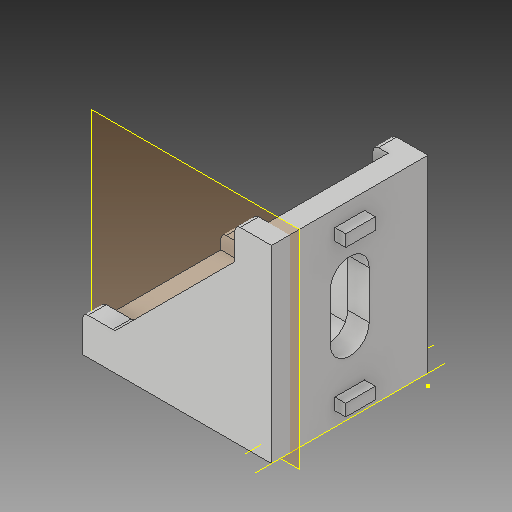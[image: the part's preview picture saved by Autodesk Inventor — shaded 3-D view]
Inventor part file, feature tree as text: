
AUTODESK INVENTOR PART (.ipt)
format: ipt  version: 2018 (Build 220112000, 112)  size: 184,832 bytes
history: native  units: mm
features: sketch x7, other x5, plane x1
ambient origin geometry x8: Origin, YZ Plane, XZ Plane, XY Plane, X Axis, Y Axis, Z Axis, Center Point
bodies: Solid1 (feature_tree)
feature tree (13):
  other  "30mm Bracket_MIR2.ipt"
  other  "Solid1::30mm Bracket_MIR2.ipt"
  other  "TaggingFeature1"
  sketch  "Sketch1"  dims[d0=10.0mm]
  sketch  "Sketch2"
  sketch  "Sketch3"
  sketch  "Sketch4"
  sketch  "Sketch5"
  sketch  "Sketch7"
  sketch  "Sketch9"
  plane  "Work Plane1"
  other  "Work Axis1"
  other  "Work Axis2"
